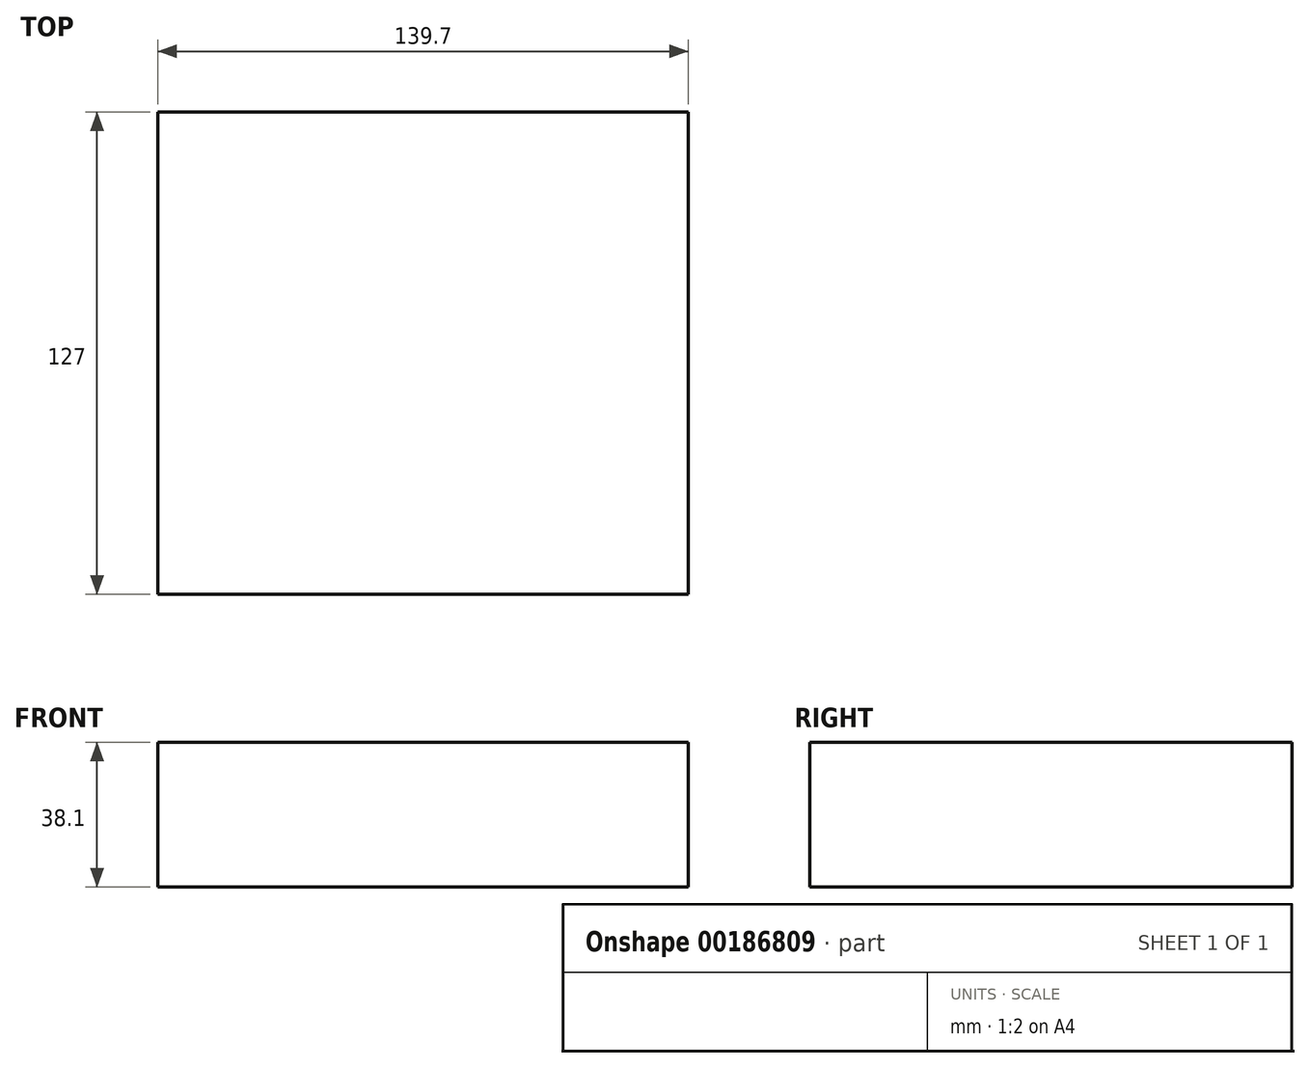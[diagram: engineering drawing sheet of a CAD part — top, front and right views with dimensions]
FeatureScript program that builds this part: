
annotation { "Feature Type Name" : "Feature", "Feature Type Description" : "" }
export const myFeature = defineFeature(function(context is Context, id is Id, definition is map)
    precondition{}
    {
        {
            var Q0;
            Q0=qCreatedBy(makeId("Front.planeOp"),FACE);
            var sketch = newSketch(context, id + "F0", { "sketchPlane" : qUnion([Q0])});
            skLineSegment(sketch, "E0.bottom", {"start": v(0, 0) * mm, "end": v(139.7, 0) * mm});
            skLineSegment(sketch, "E0.top", {"start": v(0, 38.1) * mm, "end": v(139.7, 38.1) * mm});
            skLineSegment(sketch, "E0.left", {"start": v(0, 0) * mm, "end": v(0, 38.1) * mm});
            skLineSegment(sketch, "E0.right", {"start": v(139.7, 0) * mm, "end": v(139.7, 38.1) * mm});
            skSolve(sketch);
        }
        {
            var Q0;
            Q0=makeQuery(id+"F0.imprint","IMPRINT",FACE,{"disambiguationData":[TD([[makeQuery(id+"F0.imprint","IMPRINT",EDGE,{"derivedFrom":sQuery(id+"F0.wireOp",EDGE,"E0.bottom")}),1.0]])]});
            extrude(context, id + "F1", {"entities" : qUnion([Q0]), "depth" : 127 * mm});
        }
    });
